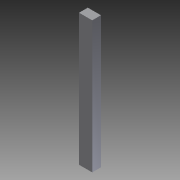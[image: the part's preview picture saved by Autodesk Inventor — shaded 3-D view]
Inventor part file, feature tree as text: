
AUTODESK INVENTOR PART (.ipt)
format: ipt  version: 2011 (Build 150239000, 239)  size: 644,096 bytes
history: native  units: in
note: dims shown in document units (in); Inventor stores cm internally (conversion verified against a paired STEP export)
features: extrude x29, sketch x29
ambient origin geometry x8: Origin, YZ Plane, XZ Plane, XY Plane, X Axis, Y Axis, Z Axis, Center Point
bodies: Solid1 (feature_tree)
feature tree (58):
  extrude  "Extrusion1"  Depth=6.75in
  extrude  "Extrusion2"  Depth=0.5in
  extrude  "Extrusion3"  Depth=0.5in
  extrude  "Extrusion4"  Depth=5.75in
  extrude  "Extrusion5"  Depth=0.5in
  extrude  "Extrusion6"  Depth=1.5in
  extrude  "Extrusion7"  Depth=1.5in
  extrude  "Extrusion8"  Depth=0.156in
  extrude  "Extrusion9"  Depth=0.25in TaperAngle=0.0deg
  extrude  "Extrusion10"  Depth=0.25in TaperAngle=0.0deg
  extrude  "Extrusion11"  Depth=0.25in TaperAngle=0.0deg
  extrude  "Extrusion12"  Depth=0.25in
  extrude  "Extrusion13"  Depth=0.25in
  extrude  "Extrusion14"  Depth=0.25in TaperAngle=0.0deg
  extrude  "Extrusion15"  Depth=3.0in
  extrude  "Extrusion16"  Depth=0.25in TaperAngle=0.0deg
  extrude  "Extrusion17"  Depth=1.0in
  extrude  "Extrusion18"  Depth=0.25in TaperAngle=0.0deg
  extrude  "Extrusion19"  Depth=0.25in TaperAngle=0.0deg
  extrude  "Extrusion20"  Depth=0.25in TaperAngle=0.0deg
  extrude  "Extrusion21"  Depth=1.0in
  extrude  "Extrusion22"  Depth=1.0in
  extrude  "Extrusion23"  Depth=2.0in
  extrude  "Extrusion24"  Depth=0.5in
  extrude  "Extrusion25"  Depth=0.5in
  extrude  "Extrusion26"  Depth=0.5in
  extrude  "Extrusion27"  Depth=0.5in
  extrude  "Extrusion28"  Depth=0.5in
  extrude  "Extrusion29"  Depth=0.5in
  sketch  "Sketch1"  dims[d0=5.2in d1=6.75in]
  sketch  "Sketch2"  dims[d2=0.25in d3=0.5in]
  sketch  "Sketch3"  dims[d4=5.7in d5=0.5in]
  sketch  "Sketch4"  dims[d6=0.5in d7=5.75in]
  sketch  "Sketch5"  dims[d8=0.375in d9=0.5in]
  sketch  "Sketch6"  dims[d10=0.25in d11=1.5in]
  sketch  "Sketch7"  dims[d12=0.25in d13=1.5in]
  sketch  "Sketch8"  dims[d14=0.25in d15=0.156in]
  sketch  "Sketch9"  dims[d16=0.156in d17=0.25in d18=0.0in]
  sketch  "Sketch10"  dims[d19=0.125in d20=0.0in d21=0.25in d22=0.0in]
  sketch  "Sketch11"  dims[d23=0.25in d24=0.0in d25=0.25in d26=0.0in]
  sketch  "Sketch12"  dims[d27=0.25in d28=0.25in]
  sketch  "Sketch13"  dims[d29=0.25in d30=0.25in]
  sketch  "Sketch14"  dims[d31=0.25in d32=0.25in d33=0.0in]
  sketch  "Sketch15"  dims[d34=1.5in d35=3.0in]
  sketch  "Sketch16"  dims[d36=1.0in d37=0.25in d38=0.0in]
  sketch  "Sketch17"  dims[d39=6.65in d40=1.0in]
  sketch  "Sketch18"  dims[d41=1.5in d42=0.25in d43=0.0in]
  sketch  "Sketch19"  dims[d44=0.25in d45=0.0in d46=0.25in d47=0.0in]
  sketch  "Sketch20"  dims[d48=1.0in d49=0.25in d50=0.0in]
  sketch  "Sketch21"  dims[d51=0.25in d52=1.0in]
  sketch  "Sketch22"  dims[d53=0.25in d54=1.0in]
  sketch  "Sketch23"  dims[d55=0.25in d56=2.0in]
  sketch  "Sketch24"  dims[d57=1.0in d58=0.5in]
  sketch  "Sketch25"  dims[d59=1.0in d60=0.5in]
  sketch  "Sketch26"  dims[d61=1.0in d62=0.5in]
  sketch  "Sketch27"  dims[d63=1.0in d64=0.5in]
  sketch  "Sketch28"  dims[d65=1.0in d66=0.5in]
  sketch  "Sketch29"  dims[d67=1.0in d68=0.5in d69=1.0in d70=0.25in d71=0.0in d72=0.25in d73=1.0in d74=1.0in d75=0.25in d76=0.0in d77=0.25in d78=0.0in d79=0.25in d80=0.25in d81=0.0in d82=0.75in d83=0.156in d84=0.156in d85=0.25in d86=0.0in d87=0.25in d88=0.0in d89=1.0in d90=1.0in d91=1.0in d92=0.25in d93=0.0in d94=1.0in d95=0.0in d96=1.0in d97=0.0in d98=1.0in d99=0.0in d100=0.5in d101=0.0in d102=0.5in d103=0.0in d104=0.25in d105=0.5in d106=0.0in d107=0.5in d108=0.0in d109=0.25in d110=0.0in d111=0.25in d112=0.0in d113=0.25in d114=0.5in d115=0.0in d116=0.25in d117=0.0in]
